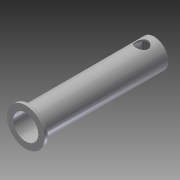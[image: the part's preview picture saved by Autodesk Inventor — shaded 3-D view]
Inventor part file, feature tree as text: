
AUTODESK INVENTOR PART (.ipt)
format: ipt  version: 2013 (Build 170138000, 138)  size: 107,008 bytes
history: native  units: in
note: dims shown in document units (in); Inventor stores cm internally (conversion verified against a paired STEP export)
features: extrude x3, sketch x3, plane x2
ambient origin geometry x8: Origin, YZ Plane, XZ Plane, XY Plane, X Axis, Y Axis, Z Axis, Center Point
bodies: Solid1 (feature_tree)
feature tree (8):
  extrude  "Extrusion1"  Depth=0.4in
  extrude  "Extrusion2"  Depth=0.6in
  plane  "Work Plane2"
  extrude  "Extrusion3"  Depth=0.25in TaperAngle=90.0deg
  sketch  "Sketch1"  dims[d0=0.45in d1=0.4in]
  sketch  "Sketch2"  dims[d2=2.0in d3=0.0in d4=0.6in]
  plane  "Work Plane1"
  sketch  "Sketch3"  dims[d5=0.05in d6=0.0in d7=90.0deg d8=0.25in d9=0.2in d10=0.2in d11=1.0in d12=0.0in]
